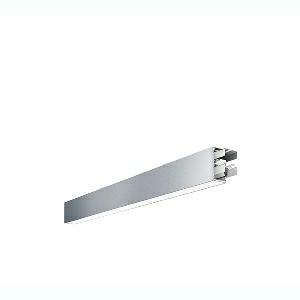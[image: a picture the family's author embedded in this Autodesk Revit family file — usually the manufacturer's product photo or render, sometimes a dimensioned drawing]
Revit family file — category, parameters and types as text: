
# Revit family: dotoo_line_-_dla_1500_840_d_sta_00807952_ccd0
name_source: partatom
category: Lighting Fixtures
units: mm (PartAtom-declared; Revit-internal decimal feet)

## family parameters
Cut with Voids When Loaded = No
Host = Face
Light Source = No
Part Type = Normal
Room Calculation Point = No
Round Connector Dimension = Use Diameter
Shared = No

## types (1)
- DOTOO.line - DLA 1500/840/D STA (1 x LED, 1350 lm, 4000K)
    Apparent Load = 13 VA
    Approval mark = CE
    CIE Flux Codes = 67 91 98 100 100
    Color Rendering = 80-89
    Color Temperature = 4000K
    Control Gear = Electronic ballast
    Default Elevation = 1800 mm
    Description = DLA 1500/840/D|Surface-mounted luminaire.|light source: LED|work equipment: Adjustable electronic ballast, digital DALI|connected load: 220-240 V, 50/60 Hz|Power consumption: approx. 13 W|luminous flux: 1350 lm|luminous efficacy: 103 lm/W|light distribution: Direct|colour temperature: Cold white, ca. 4000 K|class of protection: I|technology: Continuously dimmable|mains lead: Connector|glare control: Prism aperture|special features: DALI Load 1x, TouchDIM - dimming via standard switch, Through-wired, up to 18 m on one mains connection, Flicker-free, Suitable as emergency lighting, Start luminaire with mains connection, Mechanical and electrical connection of the individual modules without tools|
    Frequency = 50 Hz
    Height = 110 mm
    Lamp = 1 x LED
    Lamp Light Flux = 1350 lm
    Lamp count = 1
    Length = 1128 mm
    Luminous efficacy = 104 lm/W
    Manufacturer = Waldmann
    ModVariant = No
    Model = 00807952
    Mounting Place = Ceiling
    Mounting Type = Surface mounted
    Number of Poles = 1
    OnlyDefault = Yes
    Power Factor = 1
    Product Name = DOTOO.line - DLA 1500/840/D STA
    Product group = Ceiling mounted luminaire
    ProductGroupID = 3
    Protection Class = Protection class I
    Protection Degree = IP 40
    RLX_Detail_Level = 1
    RLX_Emergency_Light_Flux = 0 lm
    RLX_Emergency_Type = 0
    RLX_Emergency_Type_DB = No
    RlxData = <blob elided: 18369 chars, md5=e6e4a154>
    Socket = socket
    Standby Power = 0 W
    System Light Flux = 1350 lm
    System Power = 13 W
    Type Comments = Product without accessories
    Type Image = 114372000-00807949.jpg
    URL = http://relux.com
    VarID = ---
    Voltage = 230 V
    Voltage Range = 220-240 V
    Weight = 0.00 kg
    Width = 60 mm  [stored 0.19685 ft]

note: [stored X ft] marks values corroborated as IEEE doubles in the binary element streams (Revit-internal decimal feet)

## geometry (parser evidence)
native form markers: Blend x4, Sweep x12
no freeform markers — native parametric forms only
